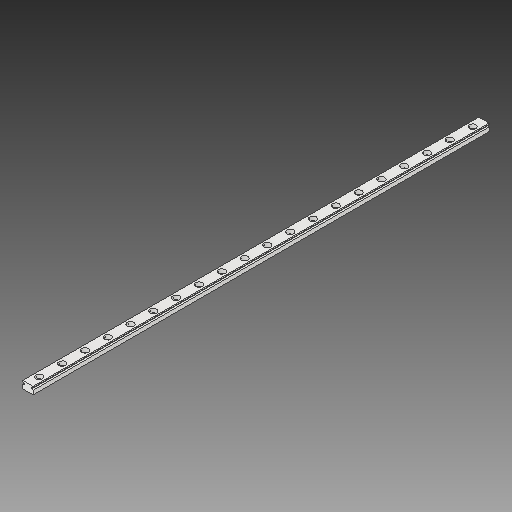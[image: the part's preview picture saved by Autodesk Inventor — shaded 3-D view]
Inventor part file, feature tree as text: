
AUTODESK INVENTOR PART (.ipt)
format: ipt  version: 2019 (Build 230136000, 136)  size: 190,976 bytes
history: imported  units: mm
features: other x3, sketch x2, imported_body x1
ambient origin geometry x8: Origin, YZ Plane, XZ Plane, XY Plane, X Axis, Y Axis, Z Axis, Center Point
bodies: Solid1 (imported_parasolid)
feature tree (6):
  other  "MGN9 Rail 400mm.ipt"
  other  "Solid1::MGN9 Rail 400mm.ipt"
  other  "TaggingFeature1"
  sketch  "Sketch1"  dims[d0=10.0mm]
  sketch  "Sketch2"
  imported_body  NMx_Import_Brep_tag  [imported B-rep: ~78 faces, bbox_mm=[9.0, 6.5, 400.0]]
